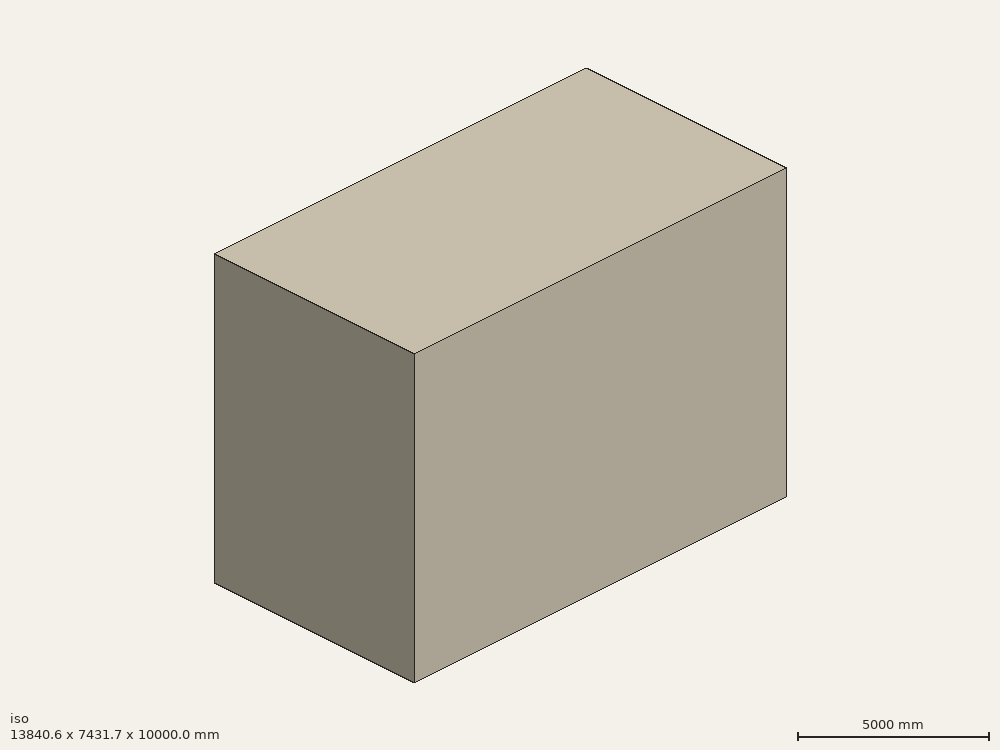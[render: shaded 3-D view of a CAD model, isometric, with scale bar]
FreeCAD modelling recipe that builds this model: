
FCSTD DOCUMENT  (FreeCAD 0.16R6706 (Git))
Label: tst
License: All rights reserved
LicenseURL: http://en.wikipedia.org/wiki/All_rights_reserved
objects: Sketcher::SketchObject×1, PartDesign::Pad×1, Part::Feature×1
note: 4 computed .brp shape members not serialized (recipe doc carries the construction recipe); baked Part::Feature solids carry a one-line shape summary decoded from their .brp

FEATURE [Sketcher::SketchObject] Sketch
  sketch-geometry (4):
    g0: LineSegment StartX=-29.4881 StartY=17.386 StartZ=0 EndX=39.7152 EndY=17.386 EndZ=0
    g1: LineSegment StartX=39.7152 StartY=17.386 StartZ=0 EndX=39.7152 EndY=-19.7724 EndZ=0
    g2: LineSegment StartX=39.7152 StartY=-19.7724 StartZ=0 EndX=-29.4881 EndY=-19.7724 EndZ=0
    g3: LineSegment StartX=-29.4881 StartY=-19.7724 StartZ=0 EndX=-29.4881 EndY=17.386 EndZ=0
  constraints (8):
    c: Coincident(g0,g1)
    c: Coincident(g1,g2)
    c: Coincident(g2,g3)
    c: Coincident(g3,g0)
    c: Horizontal(g0)
    c: Horizontal(g2)
    c: Vertical(g1)
    c: Vertical(g3)
FEATURE [PartDesign::Pad] Pad
  Length = 50
  Length2 = 100
  Sketch = -> Sketch
  Type = 0
FEATURE [Part::Feature] Pad001
  shape: bbox 13840 x 7432 x 10000 mm, 6 faces (baked)
